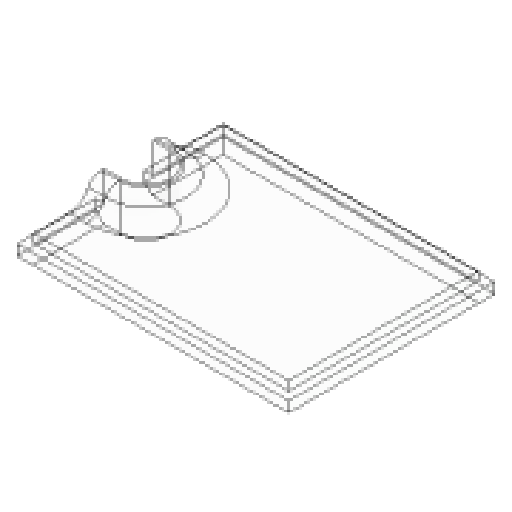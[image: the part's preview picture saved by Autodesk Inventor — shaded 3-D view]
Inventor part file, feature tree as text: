
AUTODESK INVENTOR PART (.ipt)
format: ipt  version: 2023 (Build 270158000, 158)  size: 103,936 bytes
history: native  units: mm
features: fillet x1
ambient origin geometry x8: Origin, YZ Plane, XZ Plane, XY Plane, X Axis, Y Axis, Z Axis, Center Point
bodies: Solid1 (feature_tree)
feature tree (1):
  fillet  "Fillet2"  [1 undecoded]
note: 1 required parameter value undecoded (feature->parameter linkage not recoverable at this tier; creation-order binding heuristic only, values carry confidence <= 0.55)
